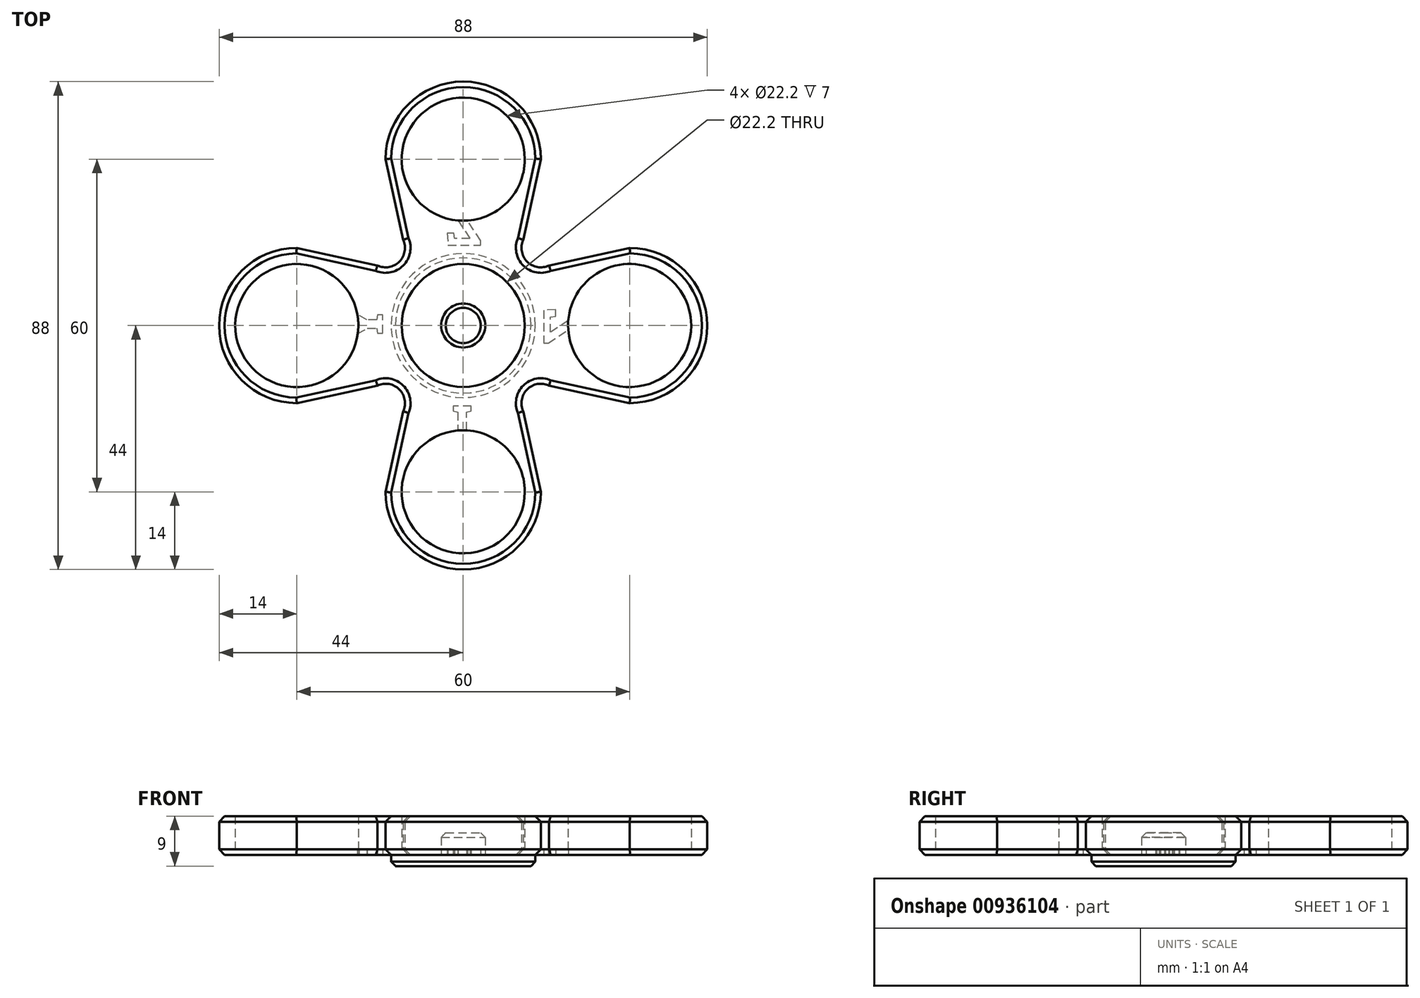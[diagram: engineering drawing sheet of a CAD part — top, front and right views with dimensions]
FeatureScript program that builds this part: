
annotation { "Feature Type Name" : "Feature", "Feature Type Description" : "" }
export const myFeature = defineFeature(function(context is Context, id is Id, definition is map)
    precondition{}
    {
        {
            var Q0;
            Q0=qCreatedBy(makeId("Top.planeOp"),FACE);
            var sketch = newSketch(context, id + "F0", { "sketchPlane" : qUnion([Q0])});
            skCircle(sketch, "E0", {"center": v(0, 0) * mm, "radius": 11.1 * mm});
            skLineSegment(sketch, "E1.bottom", {"start": v(30, -14) * mm, "end": v(-30, -14) * mm});
            skLineSegment(sketch, "E1.top", {"start": v(30, 14) * mm, "end": v(-30, 14) * mm});
            skLineSegment(sketch, "E1.left", {"start": v(30, -14) * mm, "end": v(30, 14) * mm});
            skLineSegment(sketch, "E1.right", {"start": v(-30, -14) * mm, "end": v(-30, 14) * mm});
            skCircle(sketch, "E2", {"center": v(30, 0) * mm, "radius": 14 * mm});
            skCircle(sketch, "E3", {"center": v(-30, 0) * mm, "radius": 14 * mm});
            skLineSegment(sketch, "E4.bottom", {"start": v(-14, -30) * mm, "end": v(14, -30) * mm});
            skLineSegment(sketch, "E4.top", {"start": v(-14, 30) * mm, "end": v(14, 30) * mm});
            skLineSegment(sketch, "E4.left", {"start": v(-14, -30) * mm, "end": v(-14, 30) * mm});
            skLineSegment(sketch, "E4.right", {"start": v(14, -30) * mm, "end": v(14, 30) * mm});
            skCircle(sketch, "E5", {"center": v(0, 30) * mm, "radius": 14 * mm});
            skCircle(sketch, "E6", {"center": v(0, -30) * mm, "radius": 14 * mm});
            skCircle(sketch, "E7", {"center": v(-14, 14) * mm, "radius": 3.5 * mm});
            skCircle(sketch, "E8", {"center": v(14, 14) * mm, "radius": 3.5 * mm});
            skCircle(sketch, "E9", {"center": v(14, -14) * mm, "radius": 3.5 * mm});
            skCircle(sketch, "E10", {"center": v(-14, -14) * mm, "radius": 3.5 * mm});
            skLineSegment(sketch, "E11", {"start": v(-30, -14) * mm, "end": v(-14, -10.5) * mm});
            skLineSegment(sketch, "E12", {"start": v(30, -14) * mm, "end": v(14, -10.5) * mm});
            skLineSegment(sketch, "E13", {"start": v(-10.5, -14) * mm, "end": v(-14, -30) * mm});
            skLineSegment(sketch, "E14", {"start": v(10.5, -14) * mm, "end": v(14, -30) * mm});
            skLineSegment(sketch, "E15", {"start": v(14, 30) * mm, "end": v(10.5, 14) * mm});
            skLineSegment(sketch, "E16", {"start": v(14, 10.5) * mm, "end": v(30, 14) * mm});
            skLineSegment(sketch, "E17", {"start": v(-14, 30) * mm, "end": v(-10.5, 14) * mm});
            skLineSegment(sketch, "E18", {"start": v(-14, 10.5) * mm, "end": v(-30, 14) * mm});
            skCircle(sketch, "E19", {"center": v(-30, 0) * mm, "radius": 11.1 * mm});
            skCircle(sketch, "E20", {"center": v(30, 0) * mm, "radius": 11.1 * mm});
            skCircle(sketch, "E21", {"center": v(0, 30) * mm, "radius": 11.1 * mm});
            skCircle(sketch, "E22", {"center": v(0, -30) * mm, "radius": 11.1 * mm});
            skSolve(sketch);
        }
        {
            var Q0;
            {var subQ5=sQuery(id+"F0.wireOp",EDGE,"E18");var subQ6=sQuery(id+"F0.wireOp",EDGE,"E3");var subQ7=makeQuery(id+"F0.imprint","INTERSECT",VERTEX,{"derivedFrom":[subQ6,subQ5]});Q0=makeQuery(id+"F0.imprint","IMPRINT",FACE,{"disambiguationData":[TD([[makeQuery(id+"F0.imprint","IMPRINT",EDGE,{"disambiguationData":[TD([[subQ7,1.0]])],"derivedFrom":subQ6}),-1.0]])]});}
            var Q1;
            Q1=makeQuery(id+"F0.imprint","IMPRINT",FACE,{"disambiguationData":[TD([[makeQuery(id+"F0.imprint","IMPRINT",EDGE,{"derivedFrom":sQuery(id+"F0.wireOp",EDGE,"E0")}),-1.0]])]});
            var Q2;
            {var subQ5=sQuery(id+"F0.wireOp",EDGE,"E17");var subQ9=sQuery(id+"F0.wireOp",EDGE,"E5");var subQ10=makeQuery(id+"F0.imprint","INTERSECT",VERTEX,{"derivedFrom":[subQ9,subQ5]});Q2=makeQuery(id+"F0.imprint","IMPRINT",FACE,{"disambiguationData":[TD([[makeQuery(id+"F0.imprint","IMPRINT",EDGE,{"disambiguationData":[TD([[subQ10,-1.0]])],"derivedFrom":subQ9}),-1.0]])]});}
            var Q3;
            {var subQ0=sQuery(id+"F0.wireOp",EDGE,"E1.right");Q3=makeQuery(id+"F0.imprint","IMPRINT",FACE,{"disambiguationData":[TD([[makeQuery(id+"F0.imprint","IMPRINT",EDGE,{"derivedFrom":subQ0}),-1.0]])]});}
            var Q4;
            {var subQ0=sQuery(id+"F0.wireOp",EDGE,"E1.right");Q4=makeQuery(id+"F0.imprint","IMPRINT",FACE,{"disambiguationData":[TD([[makeQuery(id+"F0.imprint","IMPRINT",EDGE,{"derivedFrom":subQ0}),1.0]])]});}
            var Q5;
            {var subQ0=sQuery(id+"F0.wireOp",EDGE,"E16");var subQ9=sQuery(id+"F0.wireOp",EDGE,"E2");var subQ10=makeQuery(id+"F0.imprint","INTERSECT",VERTEX,{"derivedFrom":[subQ9,subQ0]});Q5=makeQuery(id+"F0.imprint","IMPRINT",FACE,{"disambiguationData":[TD([[makeQuery(id+"F0.imprint","IMPRINT",EDGE,{"disambiguationData":[TD([[subQ10,-1.0]])],"derivedFrom":subQ9}),-1.0]])]});}
            var Q6;
            {var subQ5=sQuery(id+"F0.wireOp",EDGE,"E14");var subQ6=sQuery(id+"F0.wireOp",EDGE,"E6");var subQ7=makeQuery(id+"F0.imprint","INTERSECT",VERTEX,{"derivedFrom":[subQ6,subQ5]});Q6=makeQuery(id+"F0.imprint","IMPRINT",FACE,{"disambiguationData":[TD([[makeQuery(id+"F0.imprint","IMPRINT",EDGE,{"disambiguationData":[TD([[subQ7,-1.0]])],"derivedFrom":subQ6}),-1.0]])]});}
            var Q7;
            {var subQ0=sQuery(id+"F0.wireOp",EDGE,"E4.top");Q7=makeQuery(id+"F0.imprint","IMPRINT",FACE,{"disambiguationData":[TD([[makeQuery(id+"F0.imprint","IMPRINT",EDGE,{"derivedFrom":subQ0}),-1.0]])]});}
            var Q8;
            {var subQ0=sQuery(id+"F0.wireOp",EDGE,"E4.top");Q8=makeQuery(id+"F0.imprint","IMPRINT",FACE,{"disambiguationData":[TD([[makeQuery(id+"F0.imprint","IMPRINT",EDGE,{"derivedFrom":subQ0}),1.0]])]});}
            var Q9;
            {var subQ0=sQuery(id+"F0.wireOp",EDGE,"E4.bottom");Q9=makeQuery(id+"F0.imprint","IMPRINT",FACE,{"disambiguationData":[TD([[makeQuery(id+"F0.imprint","IMPRINT",EDGE,{"derivedFrom":subQ0}),1.0]])]});}
            var Q10;
            {var subQ0=sQuery(id+"F0.wireOp",EDGE,"E4.bottom");Q10=makeQuery(id+"F0.imprint","IMPRINT",FACE,{"disambiguationData":[TD([[makeQuery(id+"F0.imprint","IMPRINT",EDGE,{"derivedFrom":subQ0}),-1.0]])]});}
            var Q11;
            {var subQ0=sQuery(id+"F0.wireOp",EDGE,"E1.left");Q11=makeQuery(id+"F0.imprint","IMPRINT",FACE,{"disambiguationData":[TD([[makeQuery(id+"F0.imprint","IMPRINT",EDGE,{"derivedFrom":subQ0}),1.0]])]});}
            var Q12;
            {var subQ0=sQuery(id+"F0.wireOp",EDGE,"E1.left");Q12=makeQuery(id+"F0.imprint","IMPRINT",FACE,{"disambiguationData":[TD([[makeQuery(id+"F0.imprint","IMPRINT",EDGE,{"derivedFrom":subQ0}),-1.0]])]});}
            extrude(context, id + "F1", {"entities" : qUnion([Q0, Q1, Q2, Q3, Q4, Q5, Q6, Q7, Q8, Q9, Q10, Q11, Q12]), "depth" : 7 * mm, "offsetDistance" : 25 * mm});
        }
        {
            var Q0;
            Q0=makeQuery(id+"F1.opExtrude","CAP_EDGE",EDGE,{"disambiguationData":[OSD([sQuery(id+"F0.wireOp",EDGE,"E5")])],"isStart":false});
            var Q1;
            Q1=makeQuery(id+"F1.opExtrude","CAP_EDGE",EDGE,{"disambiguationData":[OSD([sQuery(id+"F0.wireOp",EDGE,"E15")])],"isStart":false});
            var Q2;
            Q2=makeQuery(id+"F1.opExtrude","CAP_EDGE",EDGE,{"disambiguationData":[OSD([sQuery(id+"F0.wireOp",EDGE,"E8")])],"isStart":false});
            var Q3;
            Q3=makeQuery(id+"F1.opExtrude","CAP_EDGE",EDGE,{"disambiguationData":[OSD([sQuery(id+"F0.wireOp",EDGE,"E16")])],"isStart":false});
            var Q4;
            Q4=makeQuery(id+"F1.opExtrude","CAP_EDGE",EDGE,{"disambiguationData":[OSD([sQuery(id+"F0.wireOp",EDGE,"E2")])],"isStart":false});
            var Q5;
            Q5=makeQuery(id+"F1.opExtrude","CAP_EDGE",EDGE,{"disambiguationData":[OSD([sQuery(id+"F0.wireOp",EDGE,"E12")])],"isStart":false});
            var Q6;
            Q6=makeQuery(id+"F1.opExtrude","CAP_EDGE",EDGE,{"disambiguationData":[OSD([sQuery(id+"F0.wireOp",EDGE,"E9")])],"isStart":false});
            var Q7;
            Q7=makeQuery(id+"F1.opExtrude","CAP_EDGE",EDGE,{"disambiguationData":[OSD([sQuery(id+"F0.wireOp",EDGE,"E14")])],"isStart":false});
            var Q8;
            Q8=makeQuery(id+"F1.opExtrude","CAP_EDGE",EDGE,{"disambiguationData":[OSD([sQuery(id+"F0.wireOp",EDGE,"E13")])],"isStart":false});
            var Q9;
            Q9=makeQuery(id+"F1.opExtrude","CAP_EDGE",EDGE,{"disambiguationData":[OSD([sQuery(id+"F0.wireOp",EDGE,"E10")])],"isStart":false});
            var Q10;
            Q10=makeQuery(id+"F1.opExtrude","CAP_EDGE",EDGE,{"disambiguationData":[OSD([sQuery(id+"F0.wireOp",EDGE,"E11")])],"isStart":false});
            var Q11;
            Q11=makeQuery(id+"F1.opExtrude","CAP_EDGE",EDGE,{"disambiguationData":[OSD([sQuery(id+"F0.wireOp",EDGE,"E3")])],"isStart":false});
            var Q12;
            Q12=makeQuery(id+"F1.opExtrude","CAP_EDGE",EDGE,{"disambiguationData":[OSD([sQuery(id+"F0.wireOp",EDGE,"E18")])],"isStart":false});
            var Q13;
            Q13=makeQuery(id+"F1.opExtrude","CAP_EDGE",EDGE,{"disambiguationData":[OSD([sQuery(id+"F0.wireOp",EDGE,"E7")])],"isStart":false});
            var Q14;
            Q14=makeQuery(id+"F1.opExtrude","CAP_EDGE",EDGE,{"disambiguationData":[OSD([sQuery(id+"F0.wireOp",EDGE,"E17")])],"isStart":false});
            var Q15;
            Q15=makeQuery(id+"F1.opExtrude","CAP_EDGE",EDGE,{"disambiguationData":[OSD([sQuery(id+"F0.wireOp",EDGE,"E6")])],"isStart":false});
            var Q16;
            Q16=makeQuery(id+"F1.opExtrude","CAP_EDGE",EDGE,{"disambiguationData":[OSD([sQuery(id+"F0.wireOp",EDGE,"E12")])],"isStart":true});
            var Q17;
            Q17=makeQuery(id+"F1.opExtrude","CAP_EDGE",EDGE,{"disambiguationData":[OSD([sQuery(id+"F0.wireOp",EDGE,"E2")])],"isStart":true});
            var Q18;
            Q18=makeQuery(id+"F1.opExtrude","CAP_EDGE",EDGE,{"disambiguationData":[OSD([sQuery(id+"F0.wireOp",EDGE,"E16")])],"isStart":true});
            var Q19;
            Q19=makeQuery(id+"F1.opExtrude","CAP_EDGE",EDGE,{"disambiguationData":[OSD([sQuery(id+"F0.wireOp",EDGE,"E9")])],"isStart":true});
            var Q20;
            Q20=makeQuery(id+"F1.opExtrude","CAP_EDGE",EDGE,{"disambiguationData":[OSD([sQuery(id+"F0.wireOp",EDGE,"E14")])],"isStart":true});
            var Q21;
            Q21=makeQuery(id+"F1.opExtrude","CAP_EDGE",EDGE,{"disambiguationData":[OSD([sQuery(id+"F0.wireOp",EDGE,"E6")])],"isStart":true});
            var Q22;
            Q22=makeQuery(id+"F1.opExtrude","CAP_EDGE",EDGE,{"disambiguationData":[OSD([sQuery(id+"F0.wireOp",EDGE,"E13")])],"isStart":true});
            var Q23;
            Q23=makeQuery(id+"F1.opExtrude","CAP_EDGE",EDGE,{"disambiguationData":[OSD([sQuery(id+"F0.wireOp",EDGE,"E10")])],"isStart":true});
            var Q24;
            Q24=makeQuery(id+"F1.opExtrude","CAP_EDGE",EDGE,{"disambiguationData":[OSD([sQuery(id+"F0.wireOp",EDGE,"E11")])],"isStart":true});
            var Q25;
            Q25=makeQuery(id+"F1.opExtrude","CAP_EDGE",EDGE,{"disambiguationData":[OSD([sQuery(id+"F0.wireOp",EDGE,"E3")])],"isStart":true});
            var Q26;
            Q26=makeQuery(id+"F1.opExtrude","CAP_EDGE",EDGE,{"disambiguationData":[OSD([sQuery(id+"F0.wireOp",EDGE,"E7")])],"isStart":true});
            var Q27;
            Q27=makeQuery(id+"F1.opExtrude","CAP_EDGE",EDGE,{"disambiguationData":[OSD([sQuery(id+"F0.wireOp",EDGE,"E18")])],"isStart":true});
            var Q28;
            Q28=makeQuery(id+"F1.opExtrude","CAP_EDGE",EDGE,{"disambiguationData":[OSD([sQuery(id+"F0.wireOp",EDGE,"E17")])],"isStart":true});
            var Q29;
            Q29=makeQuery(id+"F1.opExtrude","CAP_EDGE",EDGE,{"disambiguationData":[OSD([sQuery(id+"F0.wireOp",EDGE,"E8")])],"isStart":true});
            var Q30;
            Q30=makeQuery(id+"F1.opExtrude","CAP_EDGE",EDGE,{"disambiguationData":[OSD([sQuery(id+"F0.wireOp",EDGE,"E15")])],"isStart":true});
            var Q31;
            Q31=makeQuery(id+"F1.opExtrude","CAP_EDGE",EDGE,{"disambiguationData":[OSD([sQuery(id+"F0.wireOp",EDGE,"E5")])],"isStart":true});
            chamfer(context, id + "F2", {"entities" : qUnion([Q0, Q1, Q2, Q3, Q4, Q5, Q6, Q7, Q8, Q9, Q10, Q11, Q12, Q13, Q14, Q15, Q16, Q17, Q18, Q19, Q20, Q21, Q22, Q23, Q24, Q25, Q26, Q27, Q28, Q29, Q30, Q31]), "width" : 1 * mm, "tangentPropagation" : true});
        }
        {
            var Q0;
            Q0=makeQuery(id+"F1.opExtrude","CAP_FACE",FACE,{"disambiguationData":[OSD([sQuery(id+"F0.wireOp",EDGE,"E0"),sQuery(id+"F0.wireOp",EDGE,"E2"),sQuery(id+"F0.wireOp",EDGE,"E3"),sQuery(id+"F0.wireOp",EDGE,"E5"),sQuery(id+"F0.wireOp",EDGE,"E6"),sQuery(id+"F0.wireOp",EDGE,"E7"),sQuery(id+"F0.wireOp",EDGE,"E8"),sQuery(id+"F0.wireOp",EDGE,"E9"),sQuery(id+"F0.wireOp",EDGE,"E10"),sQuery(id+"F0.wireOp",EDGE,"E11"),sQuery(id+"F0.wireOp",EDGE,"E12"),sQuery(id+"F0.wireOp",EDGE,"E13"),sQuery(id+"F0.wireOp",EDGE,"E14"),sQuery(id+"F0.wireOp",EDGE,"E15"),sQuery(id+"F0.wireOp",EDGE,"E16"),sQuery(id+"F0.wireOp",EDGE,"E17"),sQuery(id+"F0.wireOp",EDGE,"E18"),sQuery(id+"F0.wireOp",EDGE,"E19"),sQuery(id+"F0.wireOp",EDGE,"E20"),sQuery(id+"F0.wireOp",EDGE,"E21"),sQuery(id+"F0.wireOp",EDGE,"E22")])],"isStart":true});
            var sketch = newSketch(context, id + "F3", { "sketchPlane" : qUnion([Q0])});
            skCircle(sketch, "E23", {"center": v(0, 0) * mm, "radius": 3.97 * mm});
            skCircle(sketch, "E24", {"center": v(0, 0) * mm, "radius": 13 * mm});
            skSolve(sketch);
        }
        {
            var Q0;
            Q0=makeQuery(id+"F3.imprint","IMPRINT",FACE,{"disambiguationData":[TD([[makeQuery(id+"F3.imprint","IMPRINT",EDGE,{"derivedFrom":sQuery(id+"F3.wireOp",EDGE,"E24")}),1.0]])]});
            var Q1;
            Q1=makeQuery(id+"F3.imprint","IMPRINT",FACE,{"disambiguationData":[TD([[makeQuery(id+"F3.imprint","IMPRINT",EDGE,{"derivedFrom":sQuery(id+"F3.wireOp",EDGE,"E23")}),-1.0]])]});
            var Q2;
            Q2=makeQuery(id+"F3.imprint","IMPRINT",FACE,{"disambiguationData":[TD([[makeQuery(id+"F3.imprint","IMPRINT",EDGE,{"derivedFrom":sQuery(id+"F3.wireOp",EDGE,"E23")}),1.0]])]});
            extrude(context, id + "F4", {"entities" : qUnion([Q0, Q1, Q2]), "depth" : 2 * mm, "offsetDistance" : 25 * mm});
        }
        {
            var Q0;
            Q0=makeQuery(id+"F3.imprint","IMPRINT",FACE,{"disambiguationData":[TD([[makeQuery(id+"F3.imprint","IMPRINT",EDGE,{"derivedFrom":sQuery(id+"F3.wireOp",EDGE,"E23")}),1.0]])]});
            extrude(context, id + "F5", {"entities" : qUnion([Q0]), "operationType" : NewBodyOperationType.ADD, "oppositeDirection" : true, "depth" : 4 * mm, "offsetDistance" : 25 * mm});
        }
        {
            var Q0;
            Q0=makeQuery(id+"F4.opExtrude","CAP_EDGE",EDGE,{"disambiguationData":[OSD([sQuery(id+"F3.wireOp",EDGE,"E24")])],"isStart":false});
            var Q1;
            Q1=makeQuery(id+"F5.opExtrude","CAP_EDGE",EDGE,{"disambiguationData":[OSD([sQuery(id+"F3.wireOp",EDGE,"E23")])],"isStart":false});
            var Q2;
            Q2=makeQuery(id+"F5.opExtrude","CAP_EDGE",EDGE,{"disambiguationData":[OSD([sQuery(id+"F3.wireOp",EDGE,"E23")])],"isStart":true});
            chamfer(context, id + "F6", {"entities" : qUnion([Q0, Q1, Q2]), "width" : .8 * mm, "tangentPropagation" : true});
        }
        {
            var Q0;
            Q0=makeQuery(id+"F1.opExtrude","CAP_FACE",FACE,{"disambiguationData":[OSD([sQuery(id+"F0.wireOp",EDGE,"E0"),sQuery(id+"F0.wireOp",EDGE,"E2"),sQuery(id+"F0.wireOp",EDGE,"E3"),sQuery(id+"F0.wireOp",EDGE,"E5"),sQuery(id+"F0.wireOp",EDGE,"E6"),sQuery(id+"F0.wireOp",EDGE,"E7"),sQuery(id+"F0.wireOp",EDGE,"E8"),sQuery(id+"F0.wireOp",EDGE,"E9"),sQuery(id+"F0.wireOp",EDGE,"E10"),sQuery(id+"F0.wireOp",EDGE,"E11"),sQuery(id+"F0.wireOp",EDGE,"E12"),sQuery(id+"F0.wireOp",EDGE,"E13"),sQuery(id+"F0.wireOp",EDGE,"E14"),sQuery(id+"F0.wireOp",EDGE,"E15"),sQuery(id+"F0.wireOp",EDGE,"E16"),sQuery(id+"F0.wireOp",EDGE,"E17"),sQuery(id+"F0.wireOp",EDGE,"E18"),sQuery(id+"F0.wireOp",EDGE,"E19"),sQuery(id+"F0.wireOp",EDGE,"E20"),sQuery(id+"F0.wireOp",EDGE,"E21"),sQuery(id+"F0.wireOp",EDGE,"E22")])],"isStart":true});
            var sketch = newSketch(context, id + "F7", { "sketchPlane" : qUnion([Q0])});
            skText(sketch, "E25", { "text": "I", "fontName": "RobotoSlab-Bold.ttf"});
            skText(sketch, "E26", { "text": "Z", "fontName": "RobotoSlab-Bold.ttf"});
            skText(sketch, "E27", { "text": "Z", "fontName": "RobotoSlab-Bold.ttf"});
            skText(sketch, "E28", { "text": "Y", "fontName": "RobotoSlab-Bold.ttf"});
            const initialGuessF7  = {"E25": [-0.00212, 0.0145, 1, 0, 0.008], "E26": [0.0145, 0.00355, 0, -1, 0.008], "E27": [0.00355, -0.0145, -1, 0, 0.008], "E28": [-0.0145, -0.00403, 0, 1, 0.008]};
            skSetInitialGuess(sketch, initialGuessF7);
            skSolve(sketch);
        }
        {
            var Q0;
            Q0 = qSketchRegion(id + "F7", true);
            extrude(context, id + "F8", {"entities" : qUnion([Q0]), "operationType" : NewBodyOperationType.REMOVE, "oppositeDirection" : true, "depth" : 1 * mm, "offsetDistance" : 25 * mm});
        }
    });
